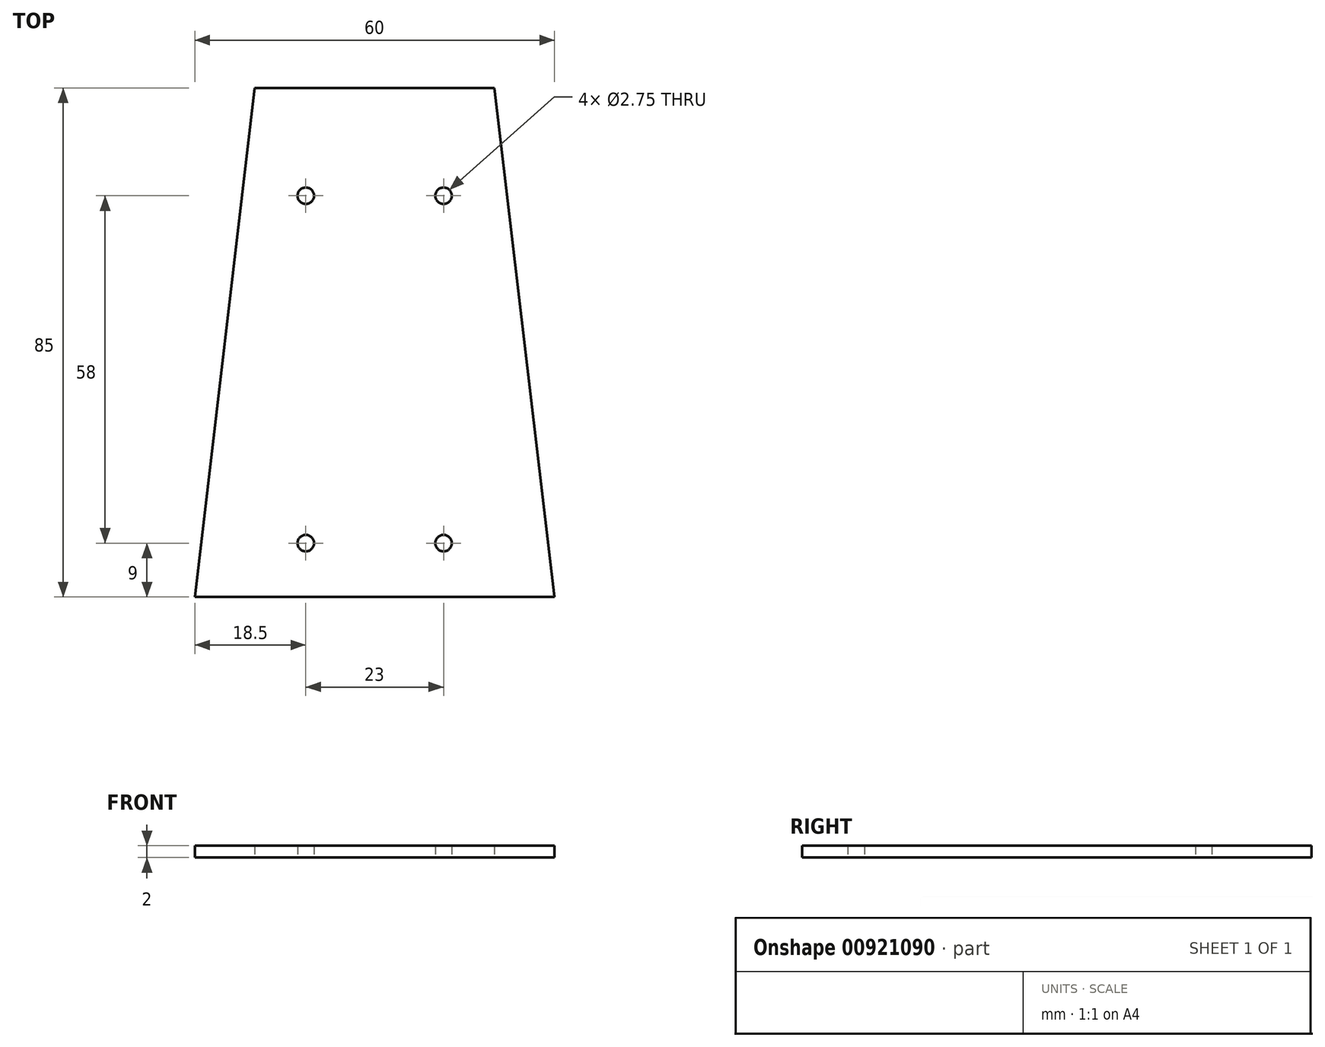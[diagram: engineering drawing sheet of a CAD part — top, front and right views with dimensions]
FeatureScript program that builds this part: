
annotation { "Feature Type Name" : "Feature", "Feature Type Description" : "" }
export const myFeature = defineFeature(function(context is Context, id is Id, definition is map)
    precondition{}
    {
        {
            var Q0;
            Q0=qCreatedBy(makeId("Top.planeOp"),FACE);
            var sketch = newSketch(context, id + "F0", { "sketchPlane" : qUnion([Q0])});
            skLineSegment(sketch, "E0", {"start": v(-20, 85) * mm, "end": v(20, 85) * mm});
            skLineSegment(sketch, "E1", {"start": v(0, 85) * mm, "end": v(0, 67) * mm});
            skCircle(sketch, "E2", {"center": v(-11.5, 67) * mm, "radius": 1.38 * mm});
            skCircle(sketch, "E3.MirrorC", {"center": v(11.5, 67) * mm, "radius": 1.38 * mm});
            skCircle(sketch, "E4", {"center": v(-11.5, 9) * mm, "radius": 1.38 * mm});
            skCircle(sketch, "E5.MirrorC", {"center": v(11.5, 9) * mm, "radius": 1.38 * mm});
            skLineSegment(sketch, "E6", {"start": v(0, 0) * mm, "end": v(-30, 0) * mm});
            skLineSegment(sketch, "E7", {"start": v(0, 0) * mm, "end": v(30, 0) * mm});
            skLineSegment(sketch, "E8", {"start": v(-20, 85) * mm, "end": v(-30, 0) * mm});
            skLineSegment(sketch, "E9", {"start": v(20, 85) * mm, "end": v(30, 0) * mm});
            skSolve(sketch);
        }
        {
            var Q0;
            Q0=makeQuery(id+"F0.imprint","IMPRINT",FACE,{"disambiguationData":[TD([[makeQuery(id+"F0.imprint","IMPRINT",EDGE,{"derivedFrom":sQuery(id+"F0.wireOp",EDGE,"E2")}),-1.0]])]});
            extrude(context, id + "F1", {"entities" : qUnion([Q0]), "depth" : 2 * mm, "offsetDistance" : 25 * mm});
        }
    });
